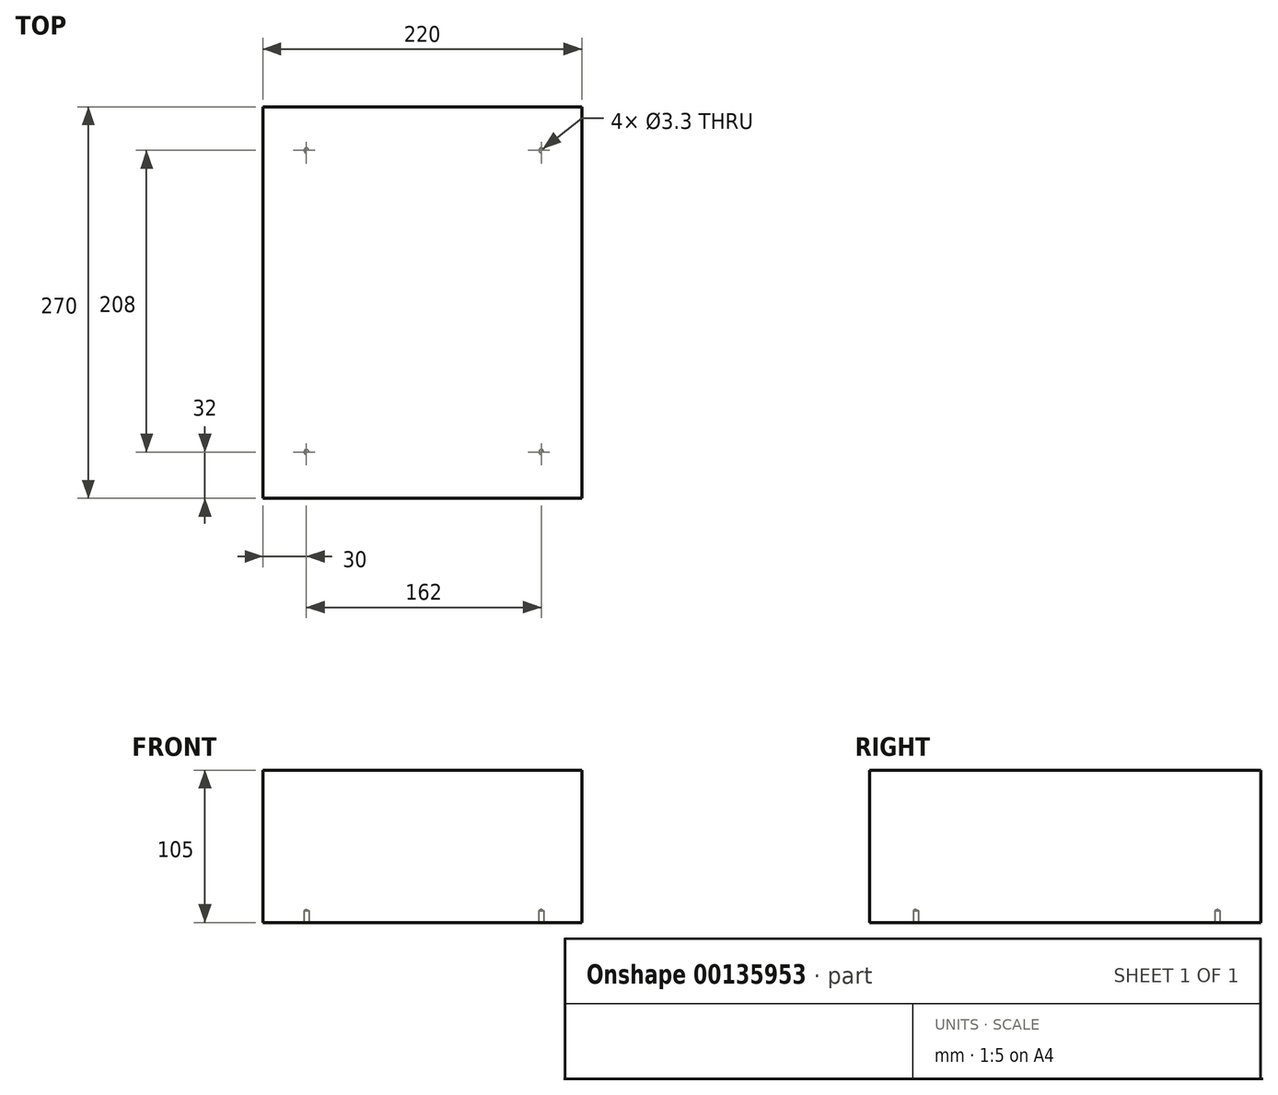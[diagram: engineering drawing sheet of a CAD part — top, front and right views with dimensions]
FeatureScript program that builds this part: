
annotation { "Feature Type Name" : "Feature", "Feature Type Description" : "" }
export const myFeature = defineFeature(function(context is Context, id is Id, definition is map)
    precondition{}
    {
        {
            var Q0;
            Q0=qCreatedBy(makeId("Top.planeOp"),FACE);
            var sketch = newSketch(context, id + "F0", { "sketchPlane" : qUnion([Q0])});
            skLineSegment(sketch, "E0.bottom", {"start": v(110, -135) * mm, "end": v(-110, -135) * mm});
            skLineSegment(sketch, "E0.top", {"start": v(110, 135) * mm, "end": v(-110, 135) * mm});
            skLineSegment(sketch, "E0.left", {"start": v(110, -135) * mm, "end": v(110, 135) * mm});
            skLineSegment(sketch, "E0.right", {"start": v(-110, -135) * mm, "end": v(-110, 135) * mm});
            skPoint(sketch, "E0.middle", {"position": v(0, 0) * mm});
            skSolve(sketch);
        }
        {
            var Q0;
            Q0 = qSketchRegion(id + "F0", true);
            extrude(context, id + "F1", {"entities" : qUnion([Q0]), "endBound" : BoundingType.SYMMETRIC, "depth" : 105 * mm});
        }
        {
            var Q0;
            Q0=makeQuery(id+"F1.opExtrude","CAP_FACE",FACE,{"disambiguationData":[OSD([sQuery(id+"F0.wireOp",EDGE,"E0.bottom"),sQuery(id+"F0.wireOp",EDGE,"E0.top"),sQuery(id+"F0.wireOp",EDGE,"E0.left"),sQuery(id+"F0.wireOp",EDGE,"E0.right")])],"isStart":true});
            var sketch = newSketch(context, id + "F2", { "sketchPlane" : qUnion([Q0])});
            skCircle(sketch, "E1", {"center": v(-80, 103) * mm, "radius": 2 * mm});
            skCircle(sketch, "E2", {"center": v(-80, -105) * mm, "radius": 2 * mm});
            skCircle(sketch, "E3", {"center": v(82, 103) * mm, "radius": 2 * mm});
            skCircle(sketch, "E4", {"center": v(82, -105) * mm, "radius": 2 * mm});
            skSolve(sketch);
        }
        {
            var Q0;
            Q0=sQuery(id+"F2.wireOp",VERTEX,"E2.center");
            var Q1;
            Q1=sQuery(id+"F2.wireOp",VERTEX,"E1.center");
            var Q2;
            Q2=sQuery(id+"F2.wireOp",VERTEX,"E3.center");
            var Q3;
            Q3=sQuery(id+"F2.wireOp",VERTEX,"E4.center");
            var Q4;
            Q4=makeQuery(id+"F1.opExtrude","SWEPT_BODY",BODY,{"disambiguationData":[OSD([sQuery(id+"F0.wireOp",EDGE,"E0.bottom"),sQuery(id+"F0.wireOp",EDGE,"E0.top"),sQuery(id+"F0.wireOp",EDGE,"E0.left"),sQuery(id+"F0.wireOp",EDGE,"E0.right")])]});
            hole(context, id + "F3", {"style" : HoleStyle.SIMPLE, "endStyle" : HoleEndStyle.BLIND, "standardTappedOrClearance" : lookupTablePath({ "standard" : "ISO", "fit" : "Normal", "size" : "M3", "type" : "Clearance" }), "standardBlindInLast" : lookupTablePath({ "fit" : "Standard", "standard" : "ISO", "size" : "M3", "type" : "Clearance" }), "holeDiameter" : 3.3 * mm, "holeDepth" : 8 * mm, "startFromSketch" : true, "locations" : qUnion([Q0, Q1, Q2, Q3]), "scope" : qUnion([Q4])});
        }
    });
